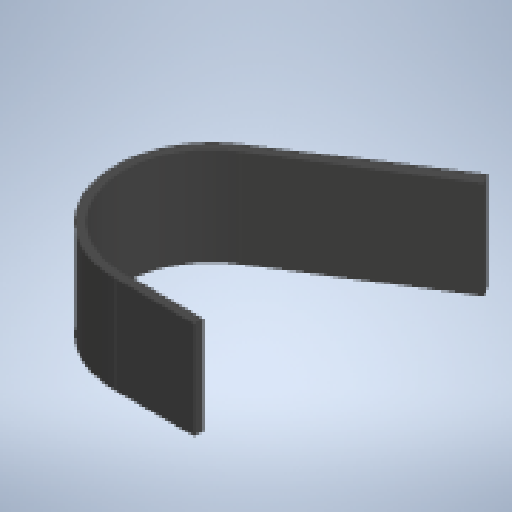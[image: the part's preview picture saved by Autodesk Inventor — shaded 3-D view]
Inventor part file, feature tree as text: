
AUTODESK INVENTOR PART (.ipt)
format: ipt  version: 2025.2 (Build 292293000, 293)  size: 262,656 bytes
history: native  units: mm
features: other x1, extrude x1, sketch x1
ambient origin geometry x8: Origin, YZ Plane, XZ Plane, XY Plane, X Axis, Y Axis, Z Axis, Center Point
bodies: Body1 (feature_tree)
feature tree (3):
  other  "ソリッド1"
  extrude  "押し出し1"  Depth=5.0mm TaperAngle=0.0deg
  sketch  "スケッチ1"
